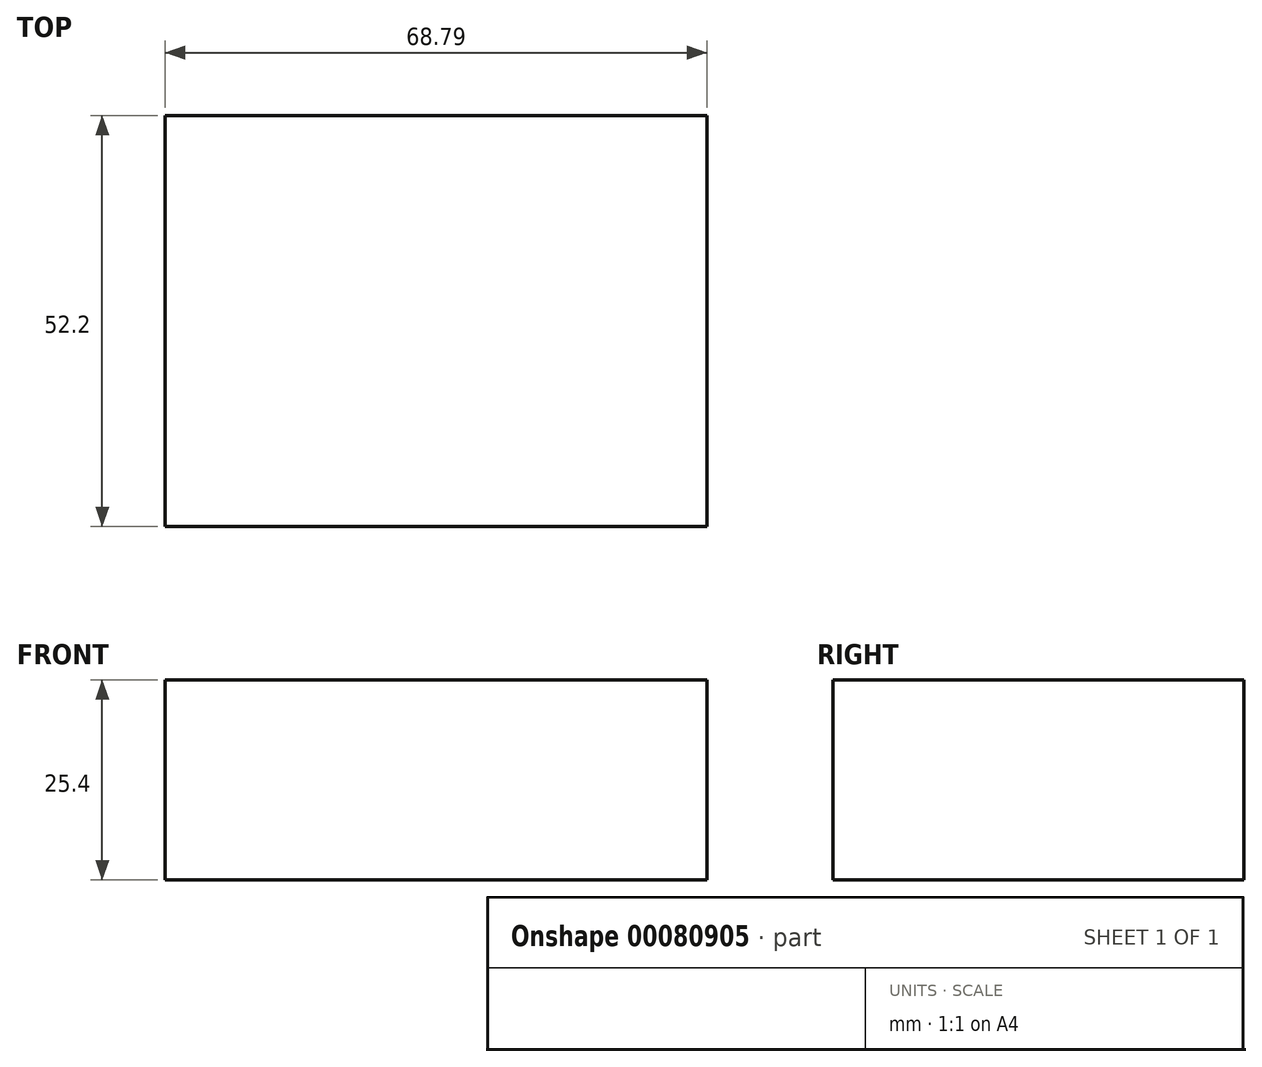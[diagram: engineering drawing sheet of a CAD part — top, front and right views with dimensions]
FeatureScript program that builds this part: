
annotation { "Feature Type Name" : "Feature", "Feature Type Description" : "" }
export const myFeature = defineFeature(function(context is Context, id is Id, definition is map)
    precondition{}
    {
        {
            var Q0;
            Q0=qCreatedBy(makeId("Top.planeOp"),FACE);
            var sketch = newSketch(context, id + "F0", { "sketchPlane" : qUnion([Q0])});
            skLineSegment(sketch, "E0.bottom", {"start": v(-33.9, 24.88) * mm, "end": v(34.88, 24.88) * mm});
            skLineSegment(sketch, "E0.top", {"start": v(-33.9, -27.32) * mm, "end": v(34.88, -27.32) * mm});
            skLineSegment(sketch, "E0.left", {"start": v(-33.9, 24.88) * mm, "end": v(-33.9, -27.32) * mm});
            skLineSegment(sketch, "E0.right", {"start": v(34.88, 24.88) * mm, "end": v(34.88, -27.32) * mm});
            skSolve(sketch);
        }
        {
            var Q0;
            Q0 = qSketchRegion(id + "F0", true);
            extrude(context, id + "F1", {"entities" : qUnion([Q0]), "depth" : 25.4 * mm});
        }
    });
